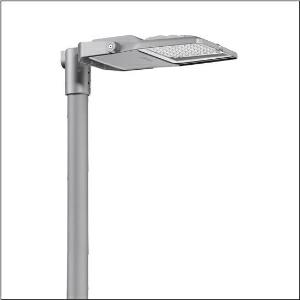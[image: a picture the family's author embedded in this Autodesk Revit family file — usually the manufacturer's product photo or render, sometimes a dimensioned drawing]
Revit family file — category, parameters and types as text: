
# Revit family: floodlight_fl_21_iq_mini___pl52_5xa7772b2d3a_55c6
name_source: partatom
category: Lighting Fixtures
units: mm (PartAtom-declared; Revit-internal decimal feet)

## family parameters
Cut with Voids When Loaded = No
Host = Face
Light Source = No
Part Type = Normal
Room Calculation Point = No
Round Connector Dimension = Use Diameter
Shared = No

## types (1)
- --- (1 x LED, 6240 lm, 45.5 W, 3000K)
    Apparent Load = 46 VA
    CIE Flux Codes = 26 60 98 100 100
    Color Rendering = 70
    Color Temperature = 3000K
    Default Elevation = 1800 mm
    Description = Floodlight FL 21 iQ mini, floodlight, primary light control with lens, of PMMA, primary optical cover: protective disc, of toughened safety glass, transparent, light distribution: PL52, light emission: direct distribution, installation type: surface-mounted, LED, High Power LED, rated luminous flux: 6.240lm, luminous efficacy: 137lm/W, light colour: 730, colour temperature: 3000K, control: Auto-Match, Temp-Guard, Night-Set, Smart-Wire, Desk-Remote (wireless, voltage-free reading and setting of iQ features in the workshop via application-optimized NFC function/RFID function), optimised constant luminous flux control (CLO 2.0), Light-Fading, Lumen-Switch, with terminal, 6-pole, mains connection: 220..240V, AC, 50/60Hz, start of lifetime: 46W, end of service life: 48W, reduction: 22W, luminaire housing, of diecast aluminium, powder-coated, Siteco® metallic grey (DB 702S), corrosivity category C5 mid according to DIN EN ISO 12944, sealing non-destructively replaceable, please order mast flange separately, mast bracket, of steel, galvanised, powder-coated, protection rating (complete): IP66, insulation class (complete): insulation class II (safety insulation), certification: CE, ENEC, VDE, protection symbol: D, impact resistance: IK08, permissible operating ambient temperature: -40..+40°C, permissible operating ambient temperature for outdoor applications: -40..+50°C, standard: DIN EN 12944, LABS conformity tested according to VDMA 24364:2018-05, packaging unit: 1 piece

Light Distribution: PL52
    Height = 70 mm
    Lamp = 1 x LED
    Lamp Light Flux = 6240 lm
    Lamp Power = 45.5 W
    Lamp count = 1
    Length = 485 mm
    Luminous efficacy = 137 lm/W
    Manufacturer = Siteco
    ModVariant = No
    Model = 5XA7772B2D3A
    Number of Poles = 1
    OnlyDefault = Yes
    Power Factor = 1
    Product Name = Floodlight FL 21 iQ mini | PL52
    Product group = floodlight | pylon annexe
    ProductGroupID = 6200
    Protection Class = Protection class II
    Protection Degree = IP 66
    RLX_Detail_Level = 1
    RLX_Emergency_Light_Flux = 0 lm
    RLX_Emergency_Type = 0
    RLX_Emergency_Type_DB = No
    RlxData = <blob elided: 101325 chars, md5=d0d3232d>
    Socket = socket
    Standby Power = 0 W
    System Light Flux = 6240 lm
    System Power = 46 W
    Type Comments = factory setting: luminous flux: 100 % | dim-lin: 254 | 463 mA
    Type Image = l_1007125.jpg
    URL = http://relux.com
    VarID = @adj_135177
    Voltage = 0 V
    Weight = 0.00 kg
    Width = 337 mm

## geometry (parser evidence)
native form markers: Blend x4, Sweep x12
no freeform markers — native parametric forms only
